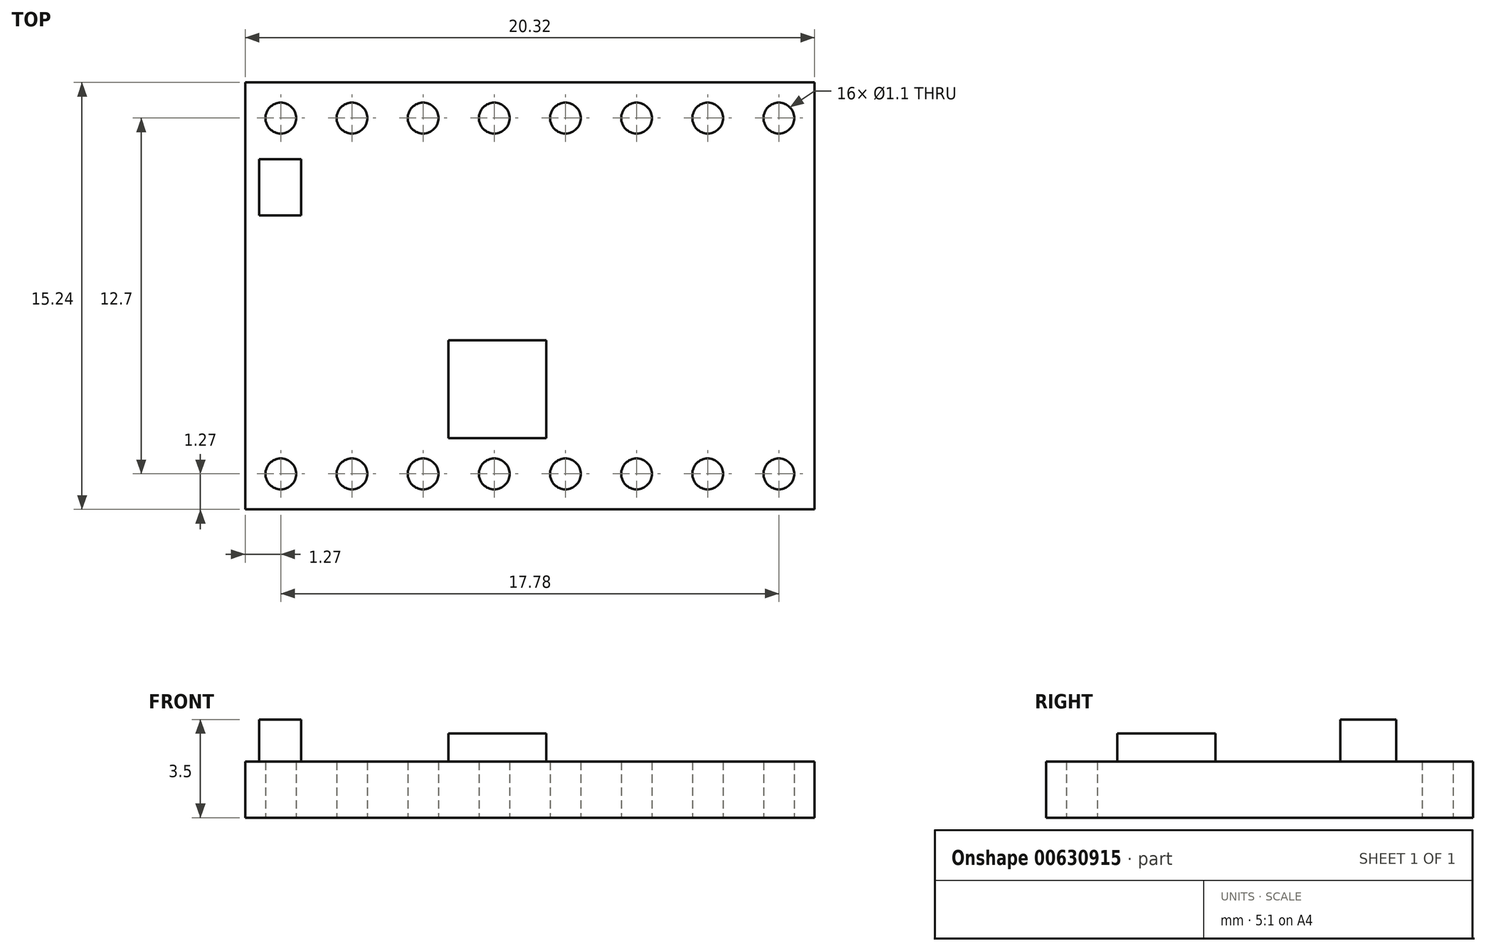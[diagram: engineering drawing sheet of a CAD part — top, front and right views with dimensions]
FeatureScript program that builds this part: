
annotation { "Feature Type Name" : "Feature", "Feature Type Description" : "" }
export const myFeature = defineFeature(function(context is Context, id is Id, definition is map)
    precondition{}
    {
        {
            var Q0;
            Q0=qCreatedBy(makeId("Top.planeOp"),FACE);
            var sketch = newSketch(context, id + "F0", { "sketchPlane" : qUnion([Q0])});
            skLineSegment(sketch, "E0.bottom", {"start": v(0, 0) * mm, "end": v(20.32, 0) * mm});
            skLineSegment(sketch, "E0.top", {"start": v(0, 15.24) * mm, "end": v(20.32, 15.24) * mm});
            skLineSegment(sketch, "E0.left", {"start": v(0, 0) * mm, "end": v(0, 15.24) * mm});
            skLineSegment(sketch, "E0.right", {"start": v(20.32, 0) * mm, "end": v(20.32, 15.24) * mm});
            skCircle(sketch, "E1", {"center": v(1.27, 1.27) * mm, "radius": 0.55 * mm});
            skCircle(sketch, "E2.0.1.0", {"center": v(1.27, 13.97) * mm, "radius": 0.55 * mm});
            skCircle(sketch, "E2.1.0.0", {"center": v(3.81, 1.27) * mm, "radius": 0.55 * mm});
            skCircle(sketch, "E2.1.1.0", {"center": v(3.81, 13.97) * mm, "radius": 0.55 * mm});
            skCircle(sketch, "E2.2.0.0", {"center": v(6.35, 1.27) * mm, "radius": 0.55 * mm});
            skCircle(sketch, "E2.2.1.0", {"center": v(6.35, 13.97) * mm, "radius": 0.55 * mm});
            skCircle(sketch, "E2.3.0.0", {"center": v(8.9, 1.27) * mm, "radius": 0.55 * mm});
            skCircle(sketch, "E2.3.1.0", {"center": v(8.9, 13.97) * mm, "radius": 0.55 * mm});
            skCircle(sketch, "E2.4.0.0", {"center": v(11.43, 1.27) * mm, "radius": 0.55 * mm});
            skCircle(sketch, "E2.4.1.0", {"center": v(11.43, 13.97) * mm, "radius": 0.55 * mm});
            skCircle(sketch, "E2.5.0.0", {"center": v(13.97, 1.27) * mm, "radius": 0.55 * mm});
            skCircle(sketch, "E2.5.1.0", {"center": v(13.97, 13.97) * mm, "radius": 0.55 * mm});
            skCircle(sketch, "E2.6.0.0", {"center": v(16.51, 1.27) * mm, "radius": 0.55 * mm});
            skCircle(sketch, "E2.6.1.0", {"center": v(16.51, 13.97) * mm, "radius": 0.55 * mm});
            skCircle(sketch, "E2.7.0.0", {"center": v(19.05, 1.27) * mm, "radius": 0.55 * mm});
            skCircle(sketch, "E2.7.1.0", {"center": v(19.05, 13.97) * mm, "radius": 0.55 * mm});
            skLineSegment(sketch, "E2.direction1", {"start": v(1.27, 1.27) * mm, "end": v(3.81, 1.27) * mm, "construction": true});
            skLineSegment(sketch, "E2.direction2", {"start": v(1.27, 1.27) * mm, "end": v(1.27, 13.97) * mm, "construction": true});
            skSolve(sketch);
        }
        {
            var Q0;
            Q0=qSketchRegion(id+"F0",true);
            extrude(context, id + "F1", {"entities" : qUnion([Q0]), "depth" : 2 * mm});
        }
        {
            var Q0;
            Q0=makeQuery(id+"F1.opExtrude","CAP_FACE",FACE,{"disambiguationData":[OSD([sQuery(id+"F0.wireOp",EDGE,"E0.bottom"),sQuery(id+"F0.wireOp",EDGE,"E0.top"),sQuery(id+"F0.wireOp",EDGE,"E0.left"),sQuery(id+"F0.wireOp",EDGE,"E0.right"),sQuery(id+"F0.wireOp",EDGE,"E1"),sQuery(id+"F0.wireOp",EDGE,"E2.0.1.0"),sQuery(id+"F0.wireOp",EDGE,"E2.1.0.0"),sQuery(id+"F0.wireOp",EDGE,"E2.1.1.0"),sQuery(id+"F0.wireOp",EDGE,"E2.2.0.0"),sQuery(id+"F0.wireOp",EDGE,"E2.2.1.0"),sQuery(id+"F0.wireOp",EDGE,"E2.3.0.0"),sQuery(id+"F0.wireOp",EDGE,"E2.3.1.0"),sQuery(id+"F0.wireOp",EDGE,"E2.4.0.0"),sQuery(id+"F0.wireOp",EDGE,"E2.4.1.0"),sQuery(id+"F0.wireOp",EDGE,"E2.5.0.0"),sQuery(id+"F0.wireOp",EDGE,"E2.5.1.0"),sQuery(id+"F0.wireOp",EDGE,"E2.6.0.0"),sQuery(id+"F0.wireOp",EDGE,"E2.6.1.0"),sQuery(id+"F0.wireOp",EDGE,"E2.7.0.0"),sQuery(id+"F0.wireOp",EDGE,"E2.7.1.0")])],"isStart":false});
            cPlane(context, id + "F2", {"entities" : qUnion([Q0]), "cplaneType" : CPlaneType.OFFSET, "offset" : 0 * mm, "width" : 150 * mm, "height" : 150 * mm});
        }
        {
            var Q0;
            Q0=qCreatedBy(id+"F2.planeOp",FACE);
            var sketch = newSketch(context, id + "F3", { "sketchPlane" : qUnion([Q0])});
            skLineSegment(sketch, "E3.bottom", {"start": v(7.25, 6.04) * mm, "end": v(10.75, 6.04) * mm});
            skLineSegment(sketch, "E3.top", {"start": v(7.25, 2.54) * mm, "end": v(10.75, 2.54) * mm});
            skLineSegment(sketch, "E3.left", {"start": v(7.25, 6.04) * mm, "end": v(7.25, 2.54) * mm});
            skLineSegment(sketch, "E3.right", {"start": v(10.75, 6.04) * mm, "end": v(10.75, 2.54) * mm});
            skLineSegment(sketch, "E4.bottom", {"start": v(0.5, 12.5) * mm, "end": v(2, 12.5) * mm});
            skLineSegment(sketch, "E4.top", {"start": v(0.5, 10.5) * mm, "end": v(2, 10.5) * mm});
            skLineSegment(sketch, "E4.left", {"start": v(0.5, 12.5) * mm, "end": v(0.5, 10.5) * mm});
            skLineSegment(sketch, "E4.right", {"start": v(2, 12.5) * mm, "end": v(2, 10.5) * mm});
            skSolve(sketch);
        }
        {
            var Q0;
            Q0=makeQuery(id+"F3.imprint","IMPRINT",FACE,{"disambiguationData":[TD([[makeQuery(id+"F3.imprint","IMPRINT",EDGE,{"derivedFrom":sQuery(id+"F3.wireOp",EDGE,"E4.bottom")}),-1.0]])]});
            extrude(context, id + "F4", {"entities" : qUnion([Q0]), "operationType" : NewBodyOperationType.ADD, "depth" : 1.5 * mm});
        }
        {
            var Q0;
            Q0=makeQuery(id+"F3.imprint","IMPRINT",FACE,{"disambiguationData":[TD([[makeQuery(id+"F3.imprint","IMPRINT",EDGE,{"derivedFrom":sQuery(id+"F3.wireOp",EDGE,"E3.bottom")}),-1.0]])]});
            extrude(context, id + "F5", {"entities" : qUnion([Q0]), "operationType" : NewBodyOperationType.ADD, "depth" : 1 * mm});
        }
    });
